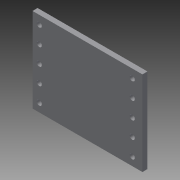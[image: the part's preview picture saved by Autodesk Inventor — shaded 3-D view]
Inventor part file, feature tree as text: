
AUTODESK INVENTOR PART (.ipt)
format: ipt  version: 2013 (Build 170138000, 138)  size: 90,112 bytes
history: native  units: mm
features: sketch x2, other x1, extrude x1, hole x1
ambient origin geometry x8: Origin, YZ Plane, XZ Plane, XY Plane, X Axis, Y Axis, Z Axis, Center Point
feature tree (5):
  other  "ソリッド1"
  extrude  "押し出し1"  Depth=65.0mm
  hole  "穴1"  [1 undecoded]
  sketch  "スケッチ1"
  sketch  "スケッチ2"
note: 1 required parameter value undecoded (feature->parameter linkage not recoverable at this tier; creation-order binding heuristic only, values carry confidence <= 0.55)
